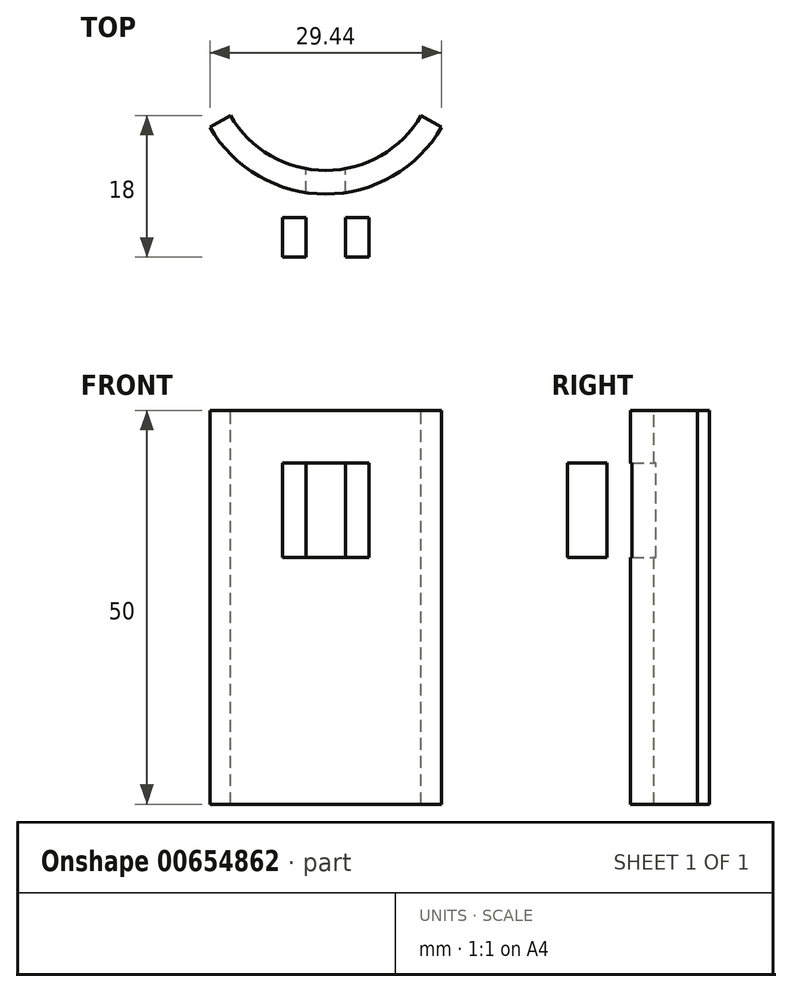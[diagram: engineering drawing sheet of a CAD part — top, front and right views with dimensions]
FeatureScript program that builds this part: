
annotation { "Feature Type Name" : "Feature", "Feature Type Description" : "" }
export const myFeature = defineFeature(function(context is Context, id is Id, definition is map)
    precondition{}
    {
        {
            var Q0;
            Q0=qCreatedBy(makeId("Top.planeOp"),FACE);
            var sketch = newSketch(context, id + "F0", { "sketchPlane" : qUnion([Q0])});
            skCircle(sketch, "E0", {"center": v(0, 0) * mm, "radius": 14 * mm});
            skCircle(sketch, "E1", {"center": v(0, 0) * mm, "radius": 12.7 * mm, "construction": true});
            skCircle(sketch, "E2.0", {"center": v(0, 0) * mm, "radius": 17 * mm});
            skLineSegment(sketch, "E3", {"start": v(0, 0) * mm, "end": v(14.72, -8.5) * mm});
            skLineSegment(sketch, "E4.MirrorCS", {"start": v(0, 0) * mm, "end": v(-14.72, -8.5) * mm});
            skSolve(sketch);
        }
        {
            var Q0;
            {var subQ0=sQuery(id+"F0.wireOp",EDGE,"E3");var subQ1=sQuery(id+"F0.wireOp",EDGE,"E0");var subQ2=makeQuery(id+"F0.imprint","INTERSECT",VERTEX,{"derivedFrom":[subQ1,subQ0]});Q0=makeQuery(id+"F0.imprint","IMPRINT",FACE,{"disambiguationData":[TD([[makeQuery(id+"F0.imprint","IMPRINT",EDGE,{"disambiguationData":[TD([[subQ2,1.0]])],"derivedFrom":subQ1}),-1.0]])]});}
            extrude(context, id + "F1", {"entities" : qUnion([Q0]), "oppositeDirection" : true, "depth" : 50 * mm, "offsetDistance" : 25 * mm});
        }
        {
            var Q0;
            Q0=qCreatedBy(makeId("Front.planeOp"),FACE);
            var sketch = newSketch(context, id + "F2", { "sketchPlane" : qUnion([Q0])});
            skLineSegment(sketch, "E5.bottom", {"start": v(2.5, -18.68) * mm, "end": v(-2.5, -18.68) * mm});
            skLineSegment(sketch, "E5.top", {"start": v(2.5, -6.68) * mm, "end": v(-2.5, -6.68) * mm});
            skLineSegment(sketch, "E5.left", {"start": v(2.5, -18.68) * mm, "end": v(2.5, -6.68) * mm});
            skLineSegment(sketch, "E5.right", {"start": v(-2.5, -18.68) * mm, "end": v(-2.5, -6.68) * mm});
            skPoint(sketch, "E5.middle", {"position": v(0, -12.68) * mm});
            skLineSegment(sketch, "E6.bottom", {"start": v(-5.5, -6.68) * mm, "end": v(5.5, -6.68) * mm});
            skLineSegment(sketch, "E6.top", {"start": v(-5.5, -18.68) * mm, "end": v(5.5, -18.68) * mm});
            skLineSegment(sketch, "E6.left", {"start": v(-5.5, -6.68) * mm, "end": v(-5.5, -18.68) * mm});
            skLineSegment(sketch, "E6.right", {"start": v(5.5, -6.68) * mm, "end": v(5.5, -18.68) * mm});
            skSolve(sketch);
        }
        {
            var Q0;
            {var subQ0=sQuery(id+"F2.wireOp",EDGE,"E5.left");Q0=makeQuery(id+"F2.imprint","IMPRINT",FACE,{"disambiguationData":[TD([[makeQuery(id+"F2.imprint","IMPRINT",EDGE,{"derivedFrom":subQ0}),1.0]])]});}
            extrude(context, id + "F3", {"entities" : qUnion([Q0]), "operationType" : NewBodyOperationType.REMOVE, "depth" : 25 * mm, "offsetDistance" : 25 * mm});
        }
        {
            var Q0;
            {var subQ0=sQuery(id+"F2.wireOp",EDGE,"E5.left");Q0=makeQuery(id+"F2.imprint","IMPRINT",FACE,{"disambiguationData":[TD([[makeQuery(id+"F2.imprint","IMPRINT",EDGE,{"derivedFrom":subQ0}),-1.0]])]});}
            var Q1;
            {var subQ0=sQuery(id+"F2.wireOp",EDGE,"E5.right");Q1=makeQuery(id+"F2.imprint","IMPRINT",FACE,{"disambiguationData":[TD([[makeQuery(id+"F2.imprint","IMPRINT",EDGE,{"derivedFrom":subQ0}),1.0]])]});}
            extrude(context, id + "F4", {"entities" : qUnion([Q0, Q1]), "depth" : 25 * mm, "offsetDistance" : 25 * mm, "hasSecondDirection" : true, "secondDirectionOppositeDirection" : false, "secondDirectionDepth" : 20 * mm});
        }
    });
